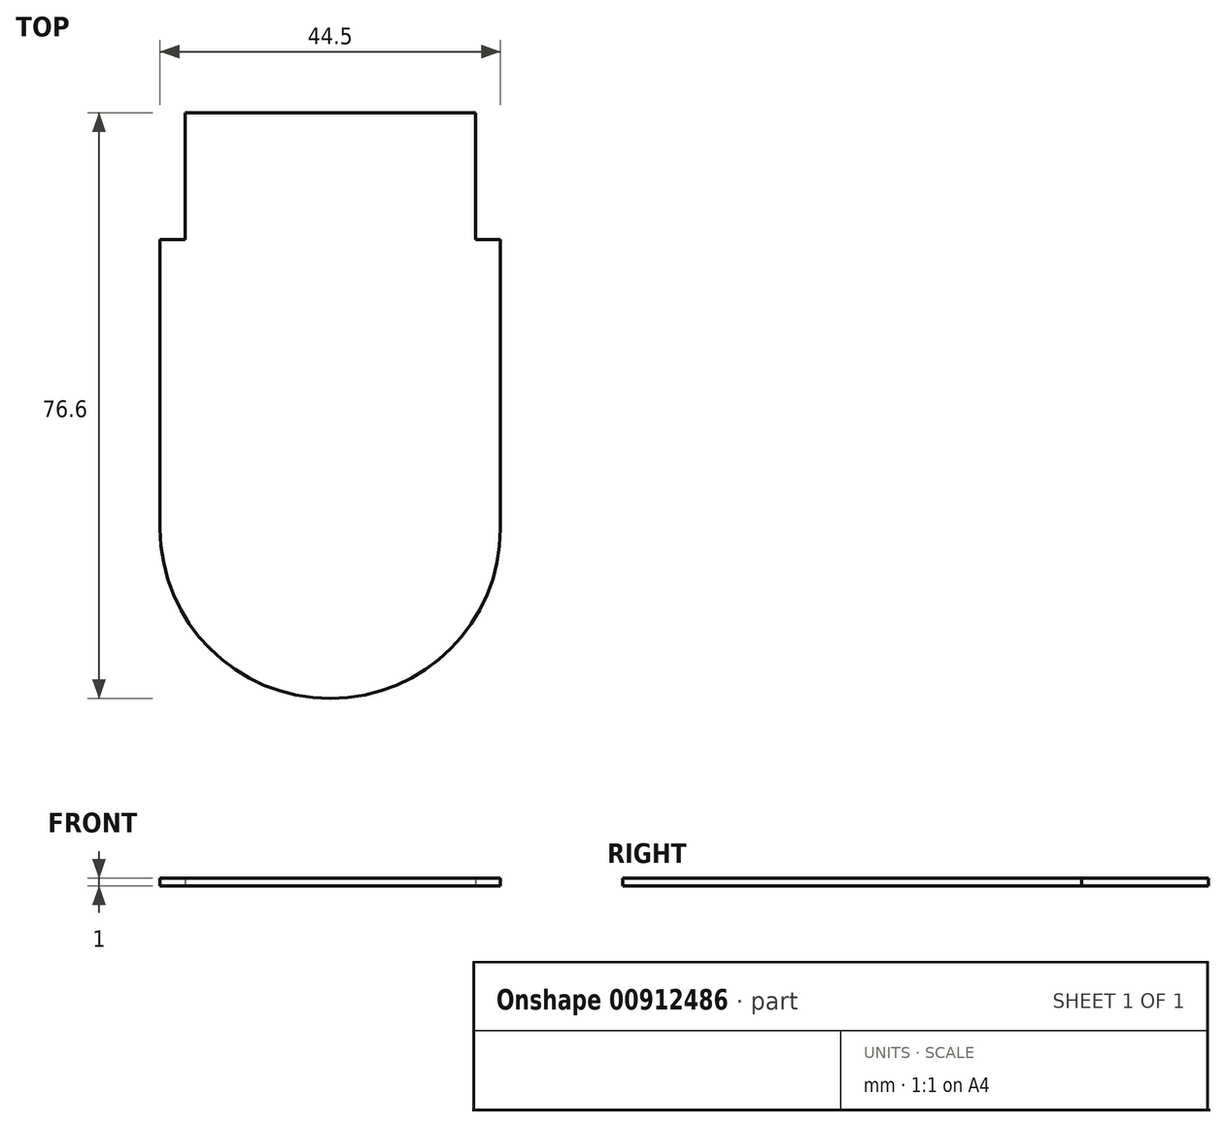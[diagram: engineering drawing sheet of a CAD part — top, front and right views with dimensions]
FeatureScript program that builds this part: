
annotation { "Feature Type Name" : "Feature", "Feature Type Description" : "" }
export const myFeature = defineFeature(function(context is Context, id is Id, definition is map)
    precondition{}
    {
        {
            var Q0;
            Q0=qCreatedBy(makeId("Top.planeOp"),FACE);
            var sketch = newSketch(context, id + "F0", { "sketchPlane" : qUnion([Q0])});
            skLineSegment(sketch, "E0.left", {"start": v(-22.25, 37.75) * mm, "end": v(-22.25, 0) * mm});
            skLineSegment(sketch, "E0.right", {"start": v(22.25, 37.75) * mm, "end": v(22.25, 0) * mm});
            skArc(sketch, "E1", {"start": v(-22.25, 0) * mm, "mid": v(0, -22.25) * mm, "end": v(22.25, 0) * mm});
            skLineSegment(sketch, "E2", {"start": v(-22.25, 37.75) * mm, "end": v(-19, 37.75) * mm});
            skLineSegment(sketch, "E3", {"start": v(-19, 37.75) * mm, "end": v(-19, 42.75) * mm});
            skLineSegment(sketch, "E4", {"start": v(22.25, 37.75) * mm, "end": v(19, 37.75) * mm});
            skPoint(sketch, "E5", {"position": v(0, 56.68) * mm});
            skLineSegment(sketch, "E6", {"start": v(-19, 42.75) * mm, "end": v(-19, 54.35) * mm});
            skLineSegment(sketch, "E7", {"start": v(19, 54.35) * mm, "end": v(-19, 54.35) * mm});
            skLineSegment(sketch, "E8", {"start": v(19, 37.75) * mm, "end": v(19, 54.35) * mm});
            skSolve(sketch);
        }
        {
            var Q0;
            {var subQ3=sQuery(id+"F0.wireOp",EDGE,"E1");Q0=makeQuery(id+"F0.imprint","IMPRINT",FACE,{"disambiguationData":[TD([[makeQuery(id+"F0.imprint","IMPRINT",EDGE,{"derivedFrom":subQ3}),1.0]])]});}
            var Q1;
            Q1=makeQuery(id+"F0.imprint","IMPRINT",FACE,{"disambiguationData":[TD([[makeQuery(id+"F0.imprint","IMPRINT",EDGE,{"derivedFrom":sQuery(id+"F0.wireOp",EDGE,"1dQ2V50v-J7Wz-5pCB-PvzS-AQyXSmz26P2g.top")}),-1.0]])]});
            extrude(context, id + "F1", {"entities" : qUnion([Q0, Q1]), "depth" : 1 * mm, "offsetDistance" : 25 * mm});
        }
    });
